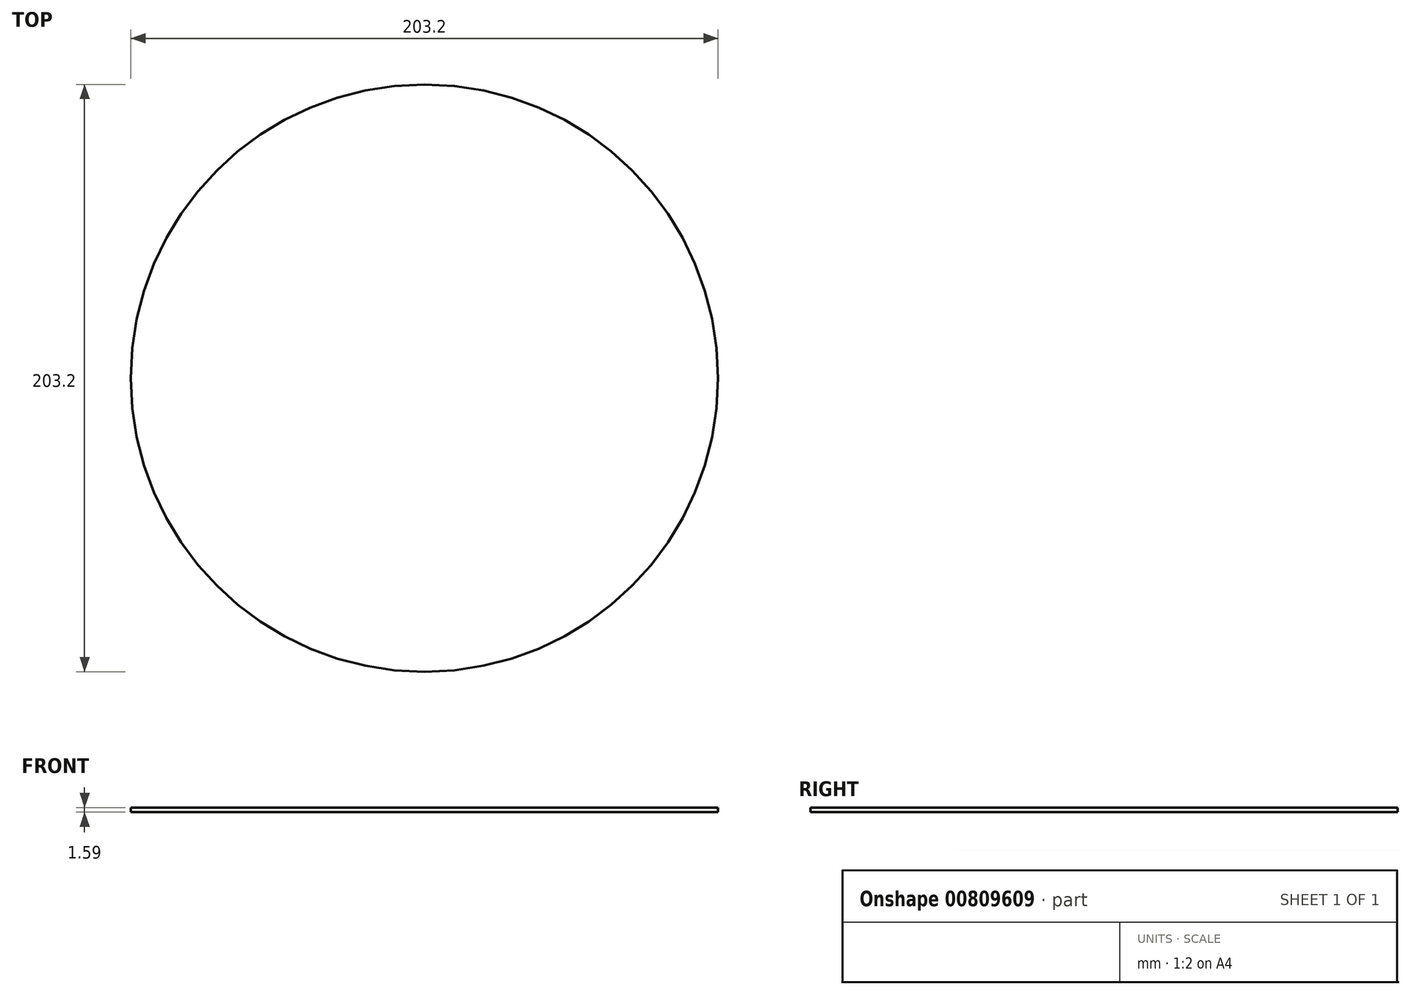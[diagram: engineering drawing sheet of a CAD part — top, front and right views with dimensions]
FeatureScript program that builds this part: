
annotation { "Feature Type Name" : "Feature", "Feature Type Description" : "" }
export const myFeature = defineFeature(function(context is Context, id is Id, definition is map)
    precondition{}
    {
        {
            var Q0;
            Q0=qCreatedBy(makeId("Top.planeOp"),FACE);
            var sketch = newSketch(context, id + "F0", { "sketchPlane" : qUnion([Q0])});
            skCircle(sketch, "E0", {"center": v(0, 0) * mm, "radius": 101.6 * mm});
            skSolve(sketch);
        }
        {
            var Q0;
            Q0=makeQuery(id+"F0.imprint","IMPRINT",FACE,{"disambiguationData":[TD([[makeQuery(id+"F0.imprint","IMPRINT",EDGE,{"derivedFrom":sQuery(id+"F0.wireOp",EDGE,"E0")}),1.0]])]});
            extrude(context, id + "F1", {"entities" : qUnion([Q0]), "oppositeDirection" : true, "depth" : 1.59 * mm, "offsetDistance" : 25.4 * mm});
        }
    });
